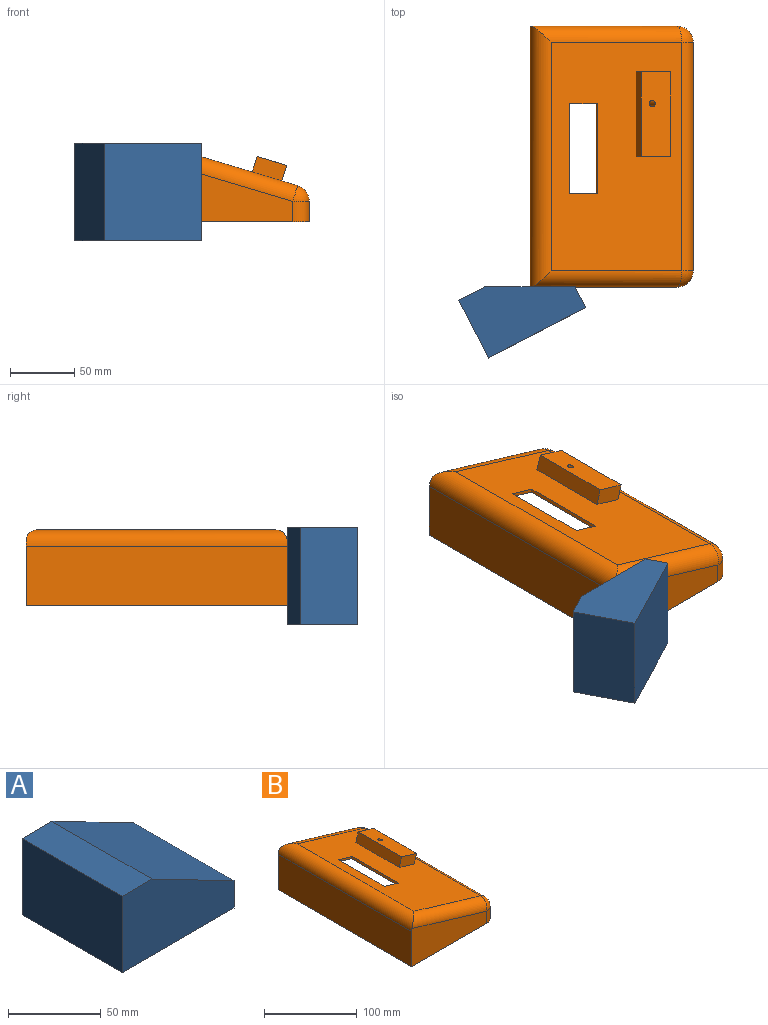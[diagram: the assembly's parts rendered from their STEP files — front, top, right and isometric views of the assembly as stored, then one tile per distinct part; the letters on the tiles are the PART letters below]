
ASSEMBLY  parts=2 mates=1
PART A: 7 faces, bbox 85.3x76.2x50.3 mm
  f0: plane 76.2x50.28mm, normal (-1,0,0), area 3831.1mm2, adj f1,f4,f5,f6
  f1: plane 85.27x76.2mm, normal (0,0,-1), area 6497.9mm2, adj f0,f2,f5,f6
  f2: plane 76.2x18.02mm, normal (1,0,0), area 1373mm2, adj f1,f3,f5,f6
  f3: plane 76.2x62.45mm, normal (0.46,0,0.89), area 5356mm2, adj f2,f4,f5,f6
  f4: plane 76.2x22.82mm, normal (0,0,1), area 1739.2mm2, adj f0,f3,f5,f6
  f5: plane 85.27x50.28mm, normal (0,-1,0), area 3280mm2, adj f0,f1,f2,f3,f4
  f6: plane 85.27x50.28mm, normal (0,1,0), area 3280mm2, adj f0,f1,f2,f3,f4
PART B: 37 faces, bbox 127x203.2x62.2 mm
  f0: plane 177.8x101.6mm, normal (0.29,0,0.96), area 15698.1mm2, adj f9,f12,f13,f14,f27,f28,f29,f30
  f1: plane 177.8x101.6mm, normal (-0.29,0,-0.96), area 17266.8mm2, adj f21,f24,f25,f26,f27,f28,f29,f30
  f2: plane 203.2x127mm, normal (0,0,-1), area 1626.7mm2, adj f3,f4,f5,f6,f7,f8,f15,f16
  f3: plane 203.2x46.43mm, normal (-1,0,0), area 9434.7mm2, adj f2,f5,f6,f14
  f4: plane 177.8x15.95mm, normal (1,0,0), area 2836.1mm2, adj f2,f7,f8,f9
  f5: plane 114.3x50.08mm, normal (0,-1,0), area 3782.2mm2, adj f2,f3,f7,f12,f14
  f6: plane 114.3x50.08mm, normal (0,1,0), area 3782.2mm2, adj f2,f3,f8,f13,f14
  f7: cylinder r=12.7mm len=15.95mm, axis (0,0,-1), area 318.2mm2, adj f2,f4,f5,f10
  f8: cylinder r=12.7mm len=15.95mm, axis (0,0,1), area 318.2mm2, adj f2,f4,f6,f11
  f9: cylinder r=12.7mm len=177.8mm, axis (0,1,0), area 2888.8mm2, adj f0,f4,f10,f11
  f10: sphere r=12.7mm, area 206.3mm2, adj f7,f9,f12
  f11: sphere r=12.7mm, area 206.3mm2, adj f8,f9,f13
  f12: cylinder r=12.7mm len=117.41mm, axis (0.96,0,-0.29), area 2277.4mm2, adj f0,f5,f10,f14
  f13: cylinder r=12.7mm len=117.41mm, axis (-0.96,0,0.29), area 2277.4mm2, adj f0,f6,f11,f14
  f14: cylinder r=12.7mm len=203.2mm, axis (0,1,0), area 4621.7mm2, adj f0,f3,f5,f6,f12,f13
  f15: plane 198.12x46.43mm, normal (1,0,0), area 9198.9mm2, adj f2,f17,f18,f26
  f16: plane 177.8x15.95mm, normal (-1,0,0), area 2836.1mm2, adj f2,f19,f20,f21
  f17: plane 111.76x49.35mm, normal (0,1,0), area 3655.8mm2, adj f2,f15,f19,f24,f26
  f18: plane 111.76x49.35mm, normal (0,-1,0), area 3655.8mm2, adj f2,f15,f20,f25,f26
  f19: cylinder r=10.16mm len=15.95mm, axis (0,0,-1), area 254.6mm2, adj f2,f16,f17,f22
  f20: cylinder r=10.16mm len=15.95mm, axis (0,0,1), area 254.6mm2, adj f2,f16,f18,f23
  f21: cylinder r=10.16mm len=177.8mm, axis (0,1,0), area 2311.1mm2, adj f1,f16,f22,f23
  f22: sphere r=10.16mm, area 132.1mm2, adj f19,f21,f24
  f23: sphere r=10.16mm, area 132.1mm2, adj f20,f21,f25
  f24: cylinder r=10.16mm len=114.25mm, axis (0.96,0,-0.29), area 1796.1mm2, adj f1,f17,f22,f26
  f25: cylinder r=10.16mm len=114.25mm, axis (-0.96,0,0.29), area 1796.1mm2, adj f1,f18,f23,f26
  f26: cylinder r=10.16mm len=198.12mm, axis (0,1,0), area 3630.7mm2, adj f1,f15,f17,f18,f24,f25
  f27: plane 22.2x8.87mm, normal (0,-1,0), area 56.9mm2, adj f0,f1,f28,f30
  f28: plane 70.17x2.43mm, normal (0.96,0,-0.29), area 178.2mm2, adj f0,f1,f27,f29
  f29: plane 22.2x8.87mm, normal (0,1,0), area 56.9mm2, adj f0,f1,f28,f30
  f30: plane 70.17x2.43mm, normal (-0.96,0,0.29), area 178.2mm2, adj f0,f1,f27,f29
  f31: plane 26.73x19.09mm, normal (0,1,0), area 306mm2, adj f0,f32,f34,f35
  f32: plane 65.96x12.16mm, normal (-0.96,0,0.29), area 837.7mm2, adj f0,f31,f33,f35
  f33: plane 26.73x19.09mm, normal (0,-1,0), area 306mm2, adj f0,f32,f34,f35
  f34: plane 65.96x12.16mm, normal (0.96,0,-0.29), area 837.7mm2, adj f0,f31,f33,f35
  f35: plane 65.96x23.08mm, normal (0.29,0,0.96), area 1568.7mm2, adj f31,f32,f33,f34,f36
  f36: cylinder r=2.55mm len=16.06mm, axis (0.29,0,0.96), area 244.4mm2, adj f1,f35
PLACE A rot(axis=(-0.95,-0.23,0.23),93.2deg) t=(-105.35,-136.99,-49.47)mm
PLACE B t=(-153.75,45.42,-60.08)mm
MATE planar A.f3 <-> B.f5  axis (0,1,0) through (-155,-157.78,-11.37)mm
